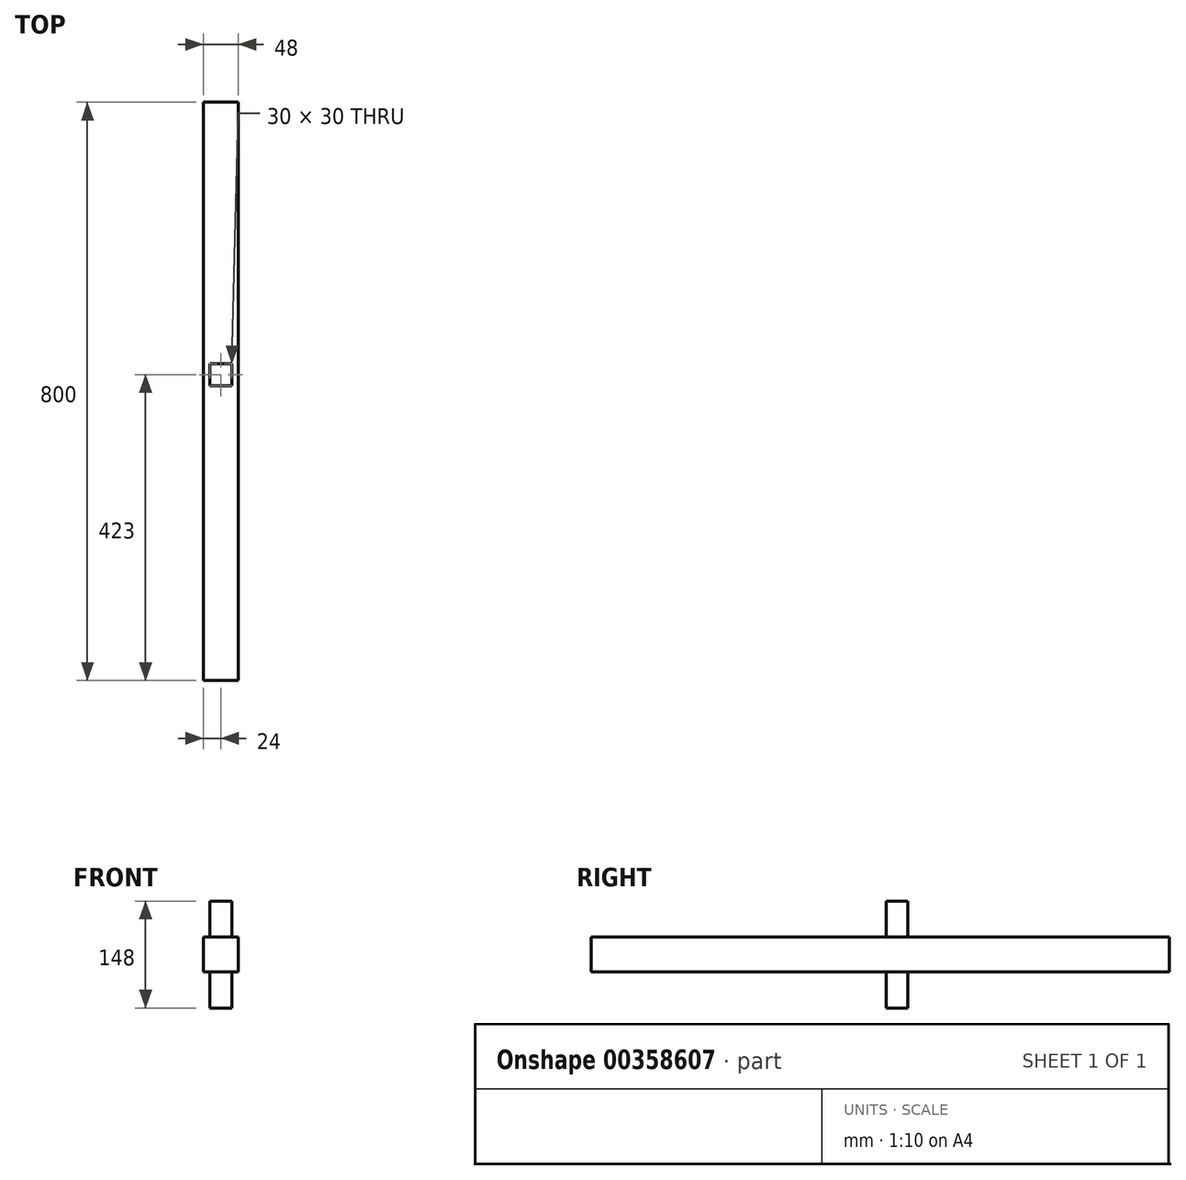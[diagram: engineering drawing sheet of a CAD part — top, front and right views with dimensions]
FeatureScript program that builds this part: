
annotation { "Feature Type Name" : "Feature", "Feature Type Description" : "" }
export const myFeature = defineFeature(function(context is Context, id is Id, definition is map)
    precondition{}
    {
        {
            var Q0;
            Q0=qCreatedBy(makeId("Front.planeOp"),FACE);
            var sketch = newSketch(context, id + "F0", { "sketchPlane" : qUnion([Q0])});
            skLineSegment(sketch, "E0.bottom", {"start": v(24, -24) * mm, "end": v(-24, -24) * mm});
            skLineSegment(sketch, "E0.top", {"start": v(24, 24) * mm, "end": v(-24, 24) * mm});
            skLineSegment(sketch, "E0.left", {"start": v(24, -24) * mm, "end": v(24, 24) * mm});
            skLineSegment(sketch, "E0.right", {"start": v(-24, -24) * mm, "end": v(-24, 24) * mm});
            skPoint(sketch, "E0.middle", {"position": v(0, 0) * mm});
            skSolve(sketch);
        }
        {
            var Q0;
            Q0 = qSketchRegion(id + "F0", true);
            extrude(context, id + "F1", {"entities" : qUnion([Q0]), "oppositeDirection" : true, "depth" : 800 * mm});
        }
        {
            var Q0;
            Q0=makeQuery(id+"F1.opExtrude","SWEPT_FACE",FACE,{"disambiguationData":[OSD([sQuery(id+"F0.wireOp",EDGE,"E0.top")])]});
            var sketch = newSketch(context, id + "F2", { "sketchPlane" : qUnion([Q0])});
            skLineSegment(sketch, "E1.bottom", {"start": v(-15, 408) * mm, "end": v(15, 408) * mm});
            skLineSegment(sketch, "E1.top", {"start": v(-15, 438) * mm, "end": v(15, 438) * mm});
            skLineSegment(sketch, "E1.left", {"start": v(-15, 408) * mm, "end": v(-15, 438) * mm});
            skLineSegment(sketch, "E1.right", {"start": v(15, 408) * mm, "end": v(15, 438) * mm});
            skPoint(sketch, "E1.middle", {"position": v(0, 423) * mm});
            skPoint(sketch, "E1.middle.positionSnap0", {"position": v(0, 800) * mm});
            skPoint(sketch, "E1.centerSnap0", {"position": v(0, 800) * mm});
            skSolve(sketch);
        }
        {
            var Q0;
            Q0 = qSketchRegion(id + "F2", true);
            extrude(context, id + "F3", {"entities" : qUnion([Q0]), "operationType" : NewBodyOperationType.ADD, "depth" : 50 * mm});
        }
        {
            var Q0;
            Q0=makeQuery(id+"F1.opExtrude","SWEPT_FACE",FACE,{"disambiguationData":[OSD([sQuery(id+"F0.wireOp",EDGE,"E0.bottom")])]});
            var sketch = newSketch(context, id + "F4", { "sketchPlane" : qUnion([Q0])});
            skLineSegment(sketch, "E2.bottom", {"start": v(-15, -438) * mm, "end": v(15, -438) * mm});
            skLineSegment(sketch, "E2.top", {"start": v(-15, -408) * mm, "end": v(15, -408) * mm});
            skLineSegment(sketch, "E2.left", {"start": v(-15, -438) * mm, "end": v(-15, -408) * mm});
            skLineSegment(sketch, "E2.right", {"start": v(15, -438) * mm, "end": v(15, -408) * mm});
            skPoint(sketch, "E2.middle", {"position": v(0, -423) * mm});
            skPoint(sketch, "E2.middle.positionSnap0", {"position": v(0, -800) * mm});
            skPoint(sketch, "E2.centerSnap0", {"position": v(0, -800) * mm});
            skSolve(sketch);
        }
        {
            var Q0;
            Q0 = qSketchRegion(id + "F4", true);
            extrude(context, id + "F5", {"entities" : qUnion([Q0]), "operationType" : NewBodyOperationType.ADD, "depth" : 50 * mm});
        }
    });
